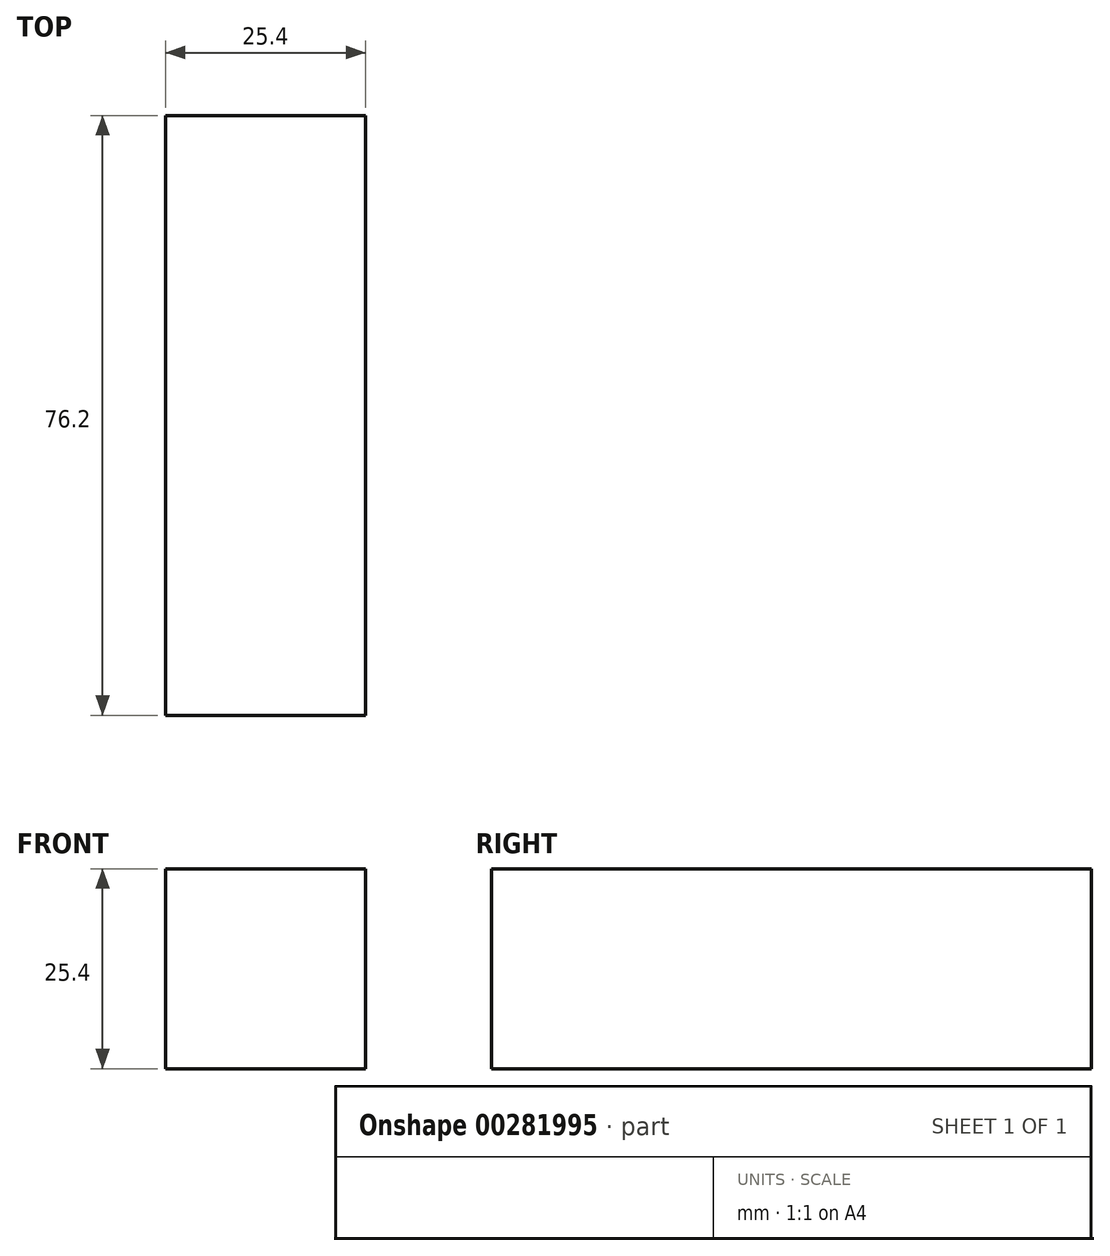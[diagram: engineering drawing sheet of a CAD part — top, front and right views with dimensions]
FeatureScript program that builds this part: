
annotation { "Feature Type Name" : "Feature", "Feature Type Description" : "" }
export const myFeature = defineFeature(function(context is Context, id is Id, definition is map)
    precondition{}
    {
        {
            var Q0;
            Q0=qCreatedBy(makeId("Front.planeOp"),FACE);
            var sketch = newSketch(context, id + "F0", { "sketchPlane" : qUnion([Q0])});
            skLineSegment(sketch, "E0.bottom", {"start": v(6.62, 0) * mm, "end": v(-18.78, 0) * mm});
            skLineSegment(sketch, "E0.top", {"start": v(6.62, 25.4) * mm, "end": v(-18.78, 25.4) * mm});
            skLineSegment(sketch, "E0.left", {"start": v(6.62, 0) * mm, "end": v(6.62, 25.4) * mm});
            skLineSegment(sketch, "E0.right", {"start": v(-18.78, 0) * mm, "end": v(-18.78, 25.4) * mm});
            skSolve(sketch);
        }
        {
            var Q0;
            Q0=makeQuery(id+"F0.imprint","IMPRINT",FACE,{"disambiguationData":[TD([[makeQuery(id+"F0.imprint","IMPRINT",EDGE,{"derivedFrom":sQuery(id+"F0.wireOp",EDGE,"E0.bottom")}),-1.0]])]});
            extrude(context, id + "F1", {"entities" : qUnion([Q0]), "depth" : 76.2 * mm});
        }
    });
